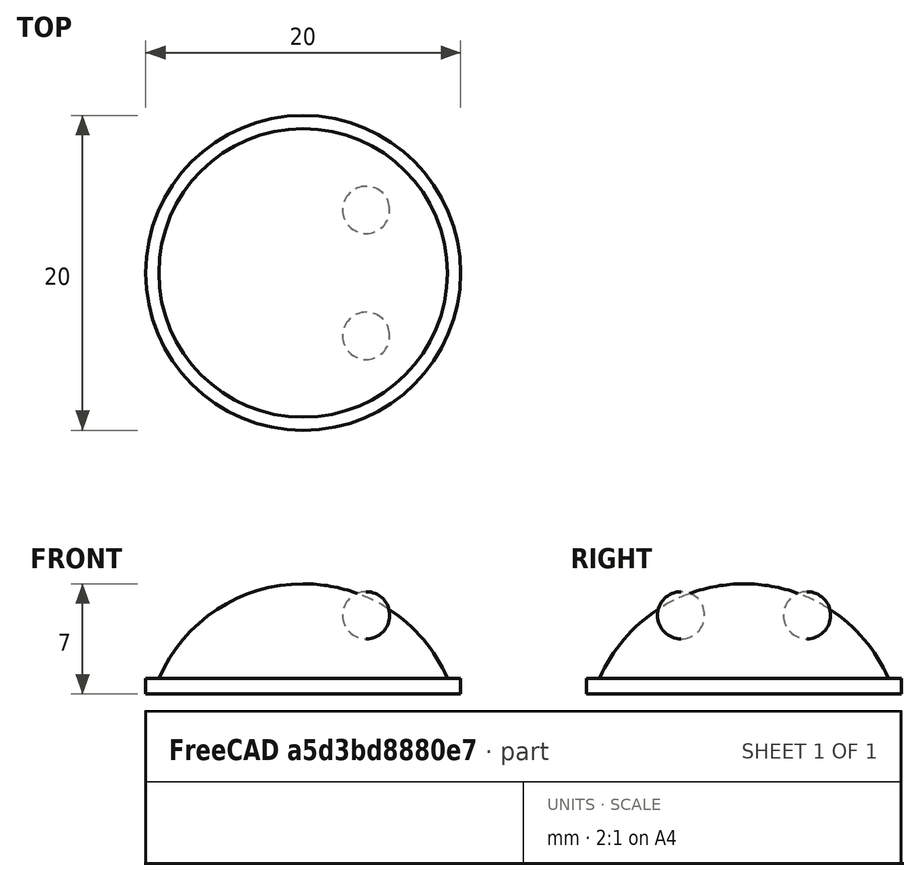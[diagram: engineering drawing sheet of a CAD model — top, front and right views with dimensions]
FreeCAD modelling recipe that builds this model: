
FCSTD DOCUMENT  (FreeCAD 1.0R39319 (Git))
Label: ojt1_t13p02_robot
License: All rights reserved
LicenseURL: https://en.wikipedia.org/wiki/All_rights_reserved
objects: Part::Sphere×3, Part::MultiFuse×2, Part::Cylinder×1
note: 6 computed .brp shape members not serialized (recipe doc carries the construction recipe); baked Part::Feature solids carry a one-line shape summary decoded from their .brp

FEATURE [Part::Sphere] Sphere  label="Esfera"
  Angle1 = 20
  Angle2 = 90
  Angle3 = 360
  AttacherType = Attacher::AttachEngine3D
  Placement = pos=(0,0,-3) rot=(0,0,1;0rad)
  Radius = 10
FEATURE [Part::Cylinder] Cylinder  label="Cilindre"
  Angle = 360
  AttacherType = Attacher::AttachEngine3D
  FirstAngle = 0
  Height = 1
  Radius = 10
  SecondAngle = 0
FEATURE [Part::Sphere] Sphere001  label="Esfera001"
  Angle1 = -90
  Angle2 = 90
  Angle3 = 360
  AttacherType = Attacher::AttachEngine3D
  Placement = pos=(4,-4,5) rot=(0,0,1;0rad)
  Radius = 1.5
FEATURE [Part::Sphere] Sphere002  label="Esfera002"
  Angle1 = -90
  Angle2 = 90
  Angle3 = 360
  AttacherType = Attacher::AttachEngine3D
  Placement = pos=(4,4,5) rot=(0,0,1;0rad)
  Radius = 1.5
FEATURE [Part::MultiFuse] Fusion
  Shapes = -> [Cylinder,Sphere]
FEATURE [Part::MultiFuse] Fusion001
  Shapes = -> [Sphere002,Sphere001]
